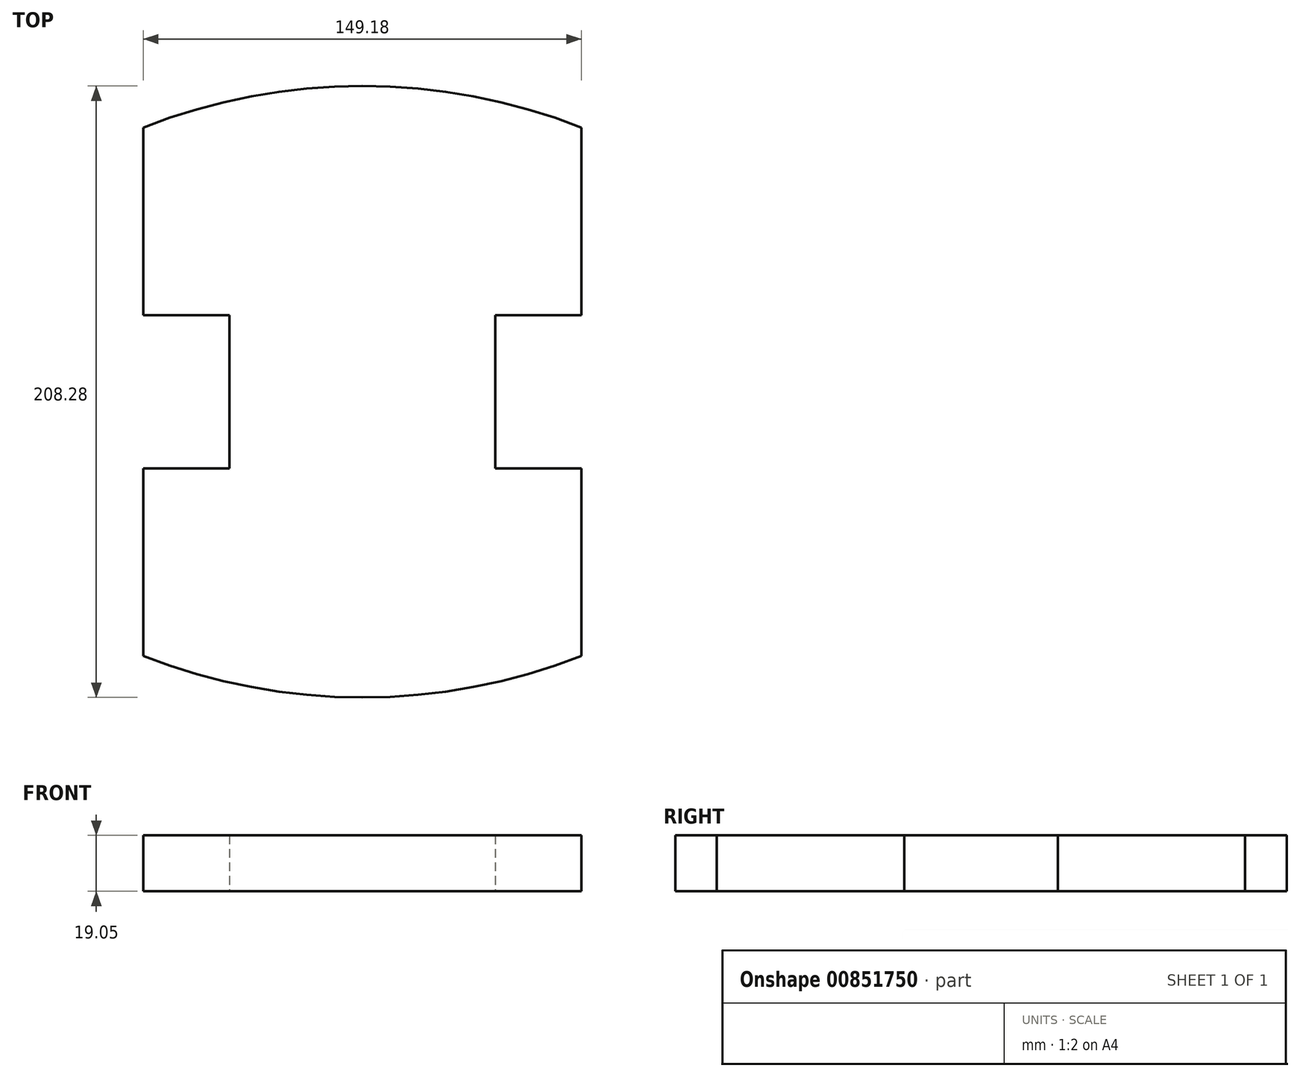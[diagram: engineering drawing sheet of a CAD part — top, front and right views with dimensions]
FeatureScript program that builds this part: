
annotation { "Feature Type Name" : "Feature", "Feature Type Description" : "" }
export const myFeature = defineFeature(function(context is Context, id is Id, definition is map)
    precondition{}
    {
        {
            var Q0;
            Q0=qCreatedBy(makeId("Top.planeOp"),FACE);
            var sketch = newSketch(context, id + "F0", { "sketchPlane" : qUnion([Q0])});
            skLineSegment(sketch, "E0", {"start": v(74.59, 90) * mm, "end": v(74.59, 26.13) * mm});
            skLineSegment(sketch, "E1", {"start": v(74.59, 26.13) * mm, "end": v(45.31, 26.13) * mm});
            skLineSegment(sketch, "E2.MirrorCS", {"start": v(-74.59, 26.13) * mm, "end": v(-45.31, 26.13) * mm});
            skLineSegment(sketch, "E3.MirrorCS", {"start": v(-74.59, 90) * mm, "end": v(-74.59, 26.13) * mm});
            skLineSegment(sketch, "E4.MirrorCS", {"start": v(74.59, -90) * mm, "end": v(74.59, -26.13) * mm});
            skLineSegment(sketch, "E5.MirrorCS", {"start": v(-74.59, -26.13) * mm, "end": v(-45.31, -26.13) * mm});
            skLineSegment(sketch, "E6.MirrorCS", {"start": v(-74.59, -90) * mm, "end": v(-74.59, -26.13) * mm});
            skLineSegment(sketch, "E7.MirrorCS", {"start": v(74.59, -26.13) * mm, "end": v(45.31, -26.13) * mm});
            skLineSegment(sketch, "E8", {"start": v(-45.31, 26.13) * mm, "end": v(-45.31, -26.13) * mm});
            skLineSegment(sketch, "E9", {"start": v(45.31, 26.13) * mm, "end": v(45.31, -26.13) * mm});
            skArc(sketch, "E10", {"start": v(74.59, 90) * mm, "mid": v(0, 104.14) * mm, "end": v(-74.59, 90) * mm});
            skArc(sketch, "E11.MirrorCS", {"start": v(74.59, -90) * mm, "mid": v(0, -104.14) * mm, "end": v(-74.59, -90) * mm});
            skSolve(sketch);
        }
        {
            var Q0;
            Q0=makeQuery(id+"F0.imprint","IMPRINT",FACE,{"disambiguationData":[TD([[makeQuery(id+"F0.imprint","IMPRINT",EDGE,{"derivedFrom":sQuery(id+"F0.wireOp",EDGE,"E0")}),-1.0]])]});
            extrude(context, id + "F1", {"entities" : qUnion([Q0]), "depth" : 19.05 * mm, "offsetDistance" : 25.4 * mm});
        }
    });
